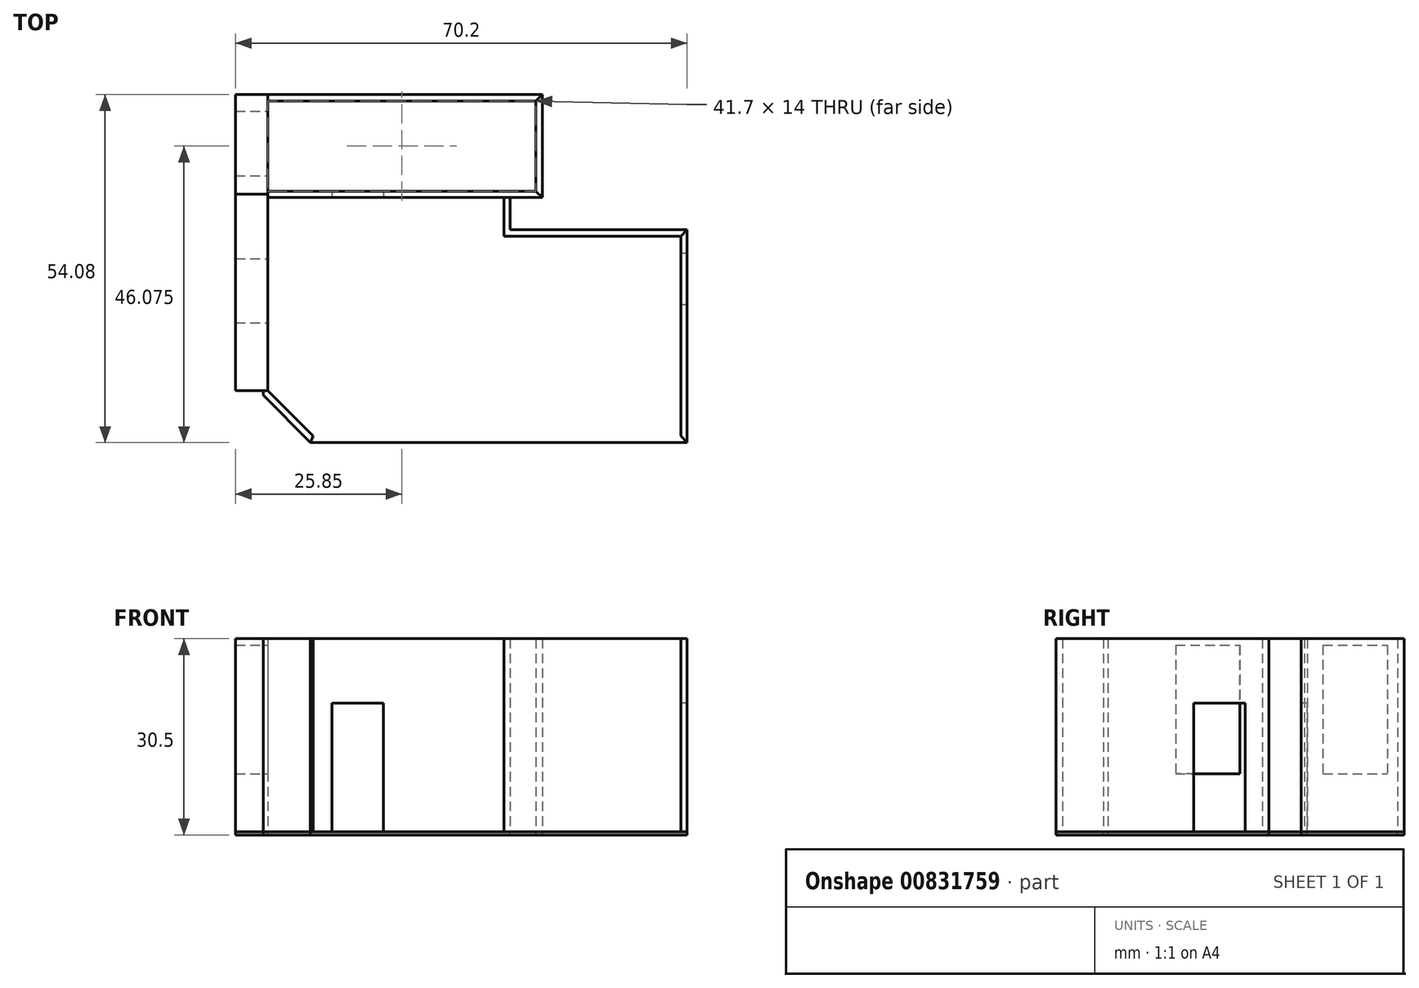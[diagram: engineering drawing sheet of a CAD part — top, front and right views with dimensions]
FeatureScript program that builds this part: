
annotation { "Feature Type Name" : "Feature", "Feature Type Description" : "" }
export const myFeature = defineFeature(function(context is Context, id is Id, definition is map)
    precondition{}
    {
        {
            var Q0;
            Q0=qCreatedBy(makeId("Top.planeOp"),FACE);
            var sketch = newSketch(context, id + "F0", { "sketchPlane" : qUnion([Q0])});
            skLineSegment(sketch, "E0", {"start": v(-36.7, -8.46) * mm, "end": v(-36.7, 21.54) * mm});
            skLineSegment(sketch, "E1", {"start": v(-36.7, 21.54) * mm, "end": v(0, 21.54) * mm});
            skLineSegment(sketch, "E2", {"start": v(0, 21.54) * mm, "end": v(0, 15.54) * mm});
            skLineSegment(sketch, "E3", {"start": v(0, 15.54) * mm, "end": v(27.5, 15.54) * mm});
            skLineSegment(sketch, "E4", {"start": v(27.5, 15.54) * mm, "end": v(27.5, -15.54) * mm});
            skLineSegment(sketch, "E5", {"start": v(27.5, -15.54) * mm, "end": v(-29.63, -15.54) * mm});
            skLineSegment(sketch, "E6", {"start": v(-29.63, -15.54) * mm, "end": v(-36.7, -8.46) * mm});
            skLineSegment(sketch, "E7", {"start": v(0, 15.54) * mm, "end": v(0, -15.54) * mm, "construction": true});
            skLineSegment(sketch, "E8", {"start": v(-36.7, 21.54) * mm, "end": v(-36.7, 36.54) * mm});
            skLineSegment(sketch, "E9", {"start": v(-36.7, 36.54) * mm, "end": v(5, 36.54) * mm});
            skLineSegment(sketch, "E10", {"start": v(5, 36.54) * mm, "end": v(5, 22.54) * mm});
            skLineSegment(sketch, "E11", {"start": v(5, 21.54) * mm, "end": v(0, 21.54) * mm});
            skLineSegment(sketch, "E12", {"start": v(-36.7, 22.54) * mm, "end": v(5, 22.54) * mm});
            skLineSegment(sketch, "E13.0", {"start": v(6, 37.54) * mm, "end": v(6, 21.54) * mm});
            skLineSegment(sketch, "E13.1", {"start": v(-36.7, 37.54) * mm, "end": v(6, 37.54) * mm});
            skLineSegment(sketch, "E14", {"start": v(-36.7, 37.54) * mm, "end": v(-36.7, 36.54) * mm});
            skLineSegment(sketch, "E15", {"start": v(6, 21.54) * mm, "end": v(5, 21.54) * mm});
            skLineSegment(sketch, "E16.0", {"start": v(-30.04, -16.54) * mm, "end": v(-37.4, -9.17) * mm});
            skLineSegment(sketch, "E16.1", {"start": v(1, 21.54) * mm, "end": v(1, 16.54) * mm});
            skLineSegment(sketch, "E16.2", {"start": v(1, 16.54) * mm, "end": v(28.5, 16.54) * mm});
            skLineSegment(sketch, "E16.3", {"start": v(28.5, 16.54) * mm, "end": v(28.5, -16.54) * mm});
            skLineSegment(sketch, "E16.4", {"start": v(28.5, -16.54) * mm, "end": v(-30.04, -16.54) * mm});
            skLineSegment(sketch, "E17", {"start": v(-36.7, -8.46) * mm, "end": v(-37.4, -9.17) * mm, "construction": true});
            skLineSegment(sketch, "E18", {"start": v(-36.7, 37.54) * mm, "end": v(-41.7, 37.54) * mm});
            skLineSegment(sketch, "E19", {"start": v(-41.7, 37.54) * mm, "end": v(-41.7, -8.46) * mm});
            skLineSegment(sketch, "E20", {"start": v(-41.7, -8.46) * mm, "end": v(-37.4, -8.46) * mm});
            skLineSegment(sketch, "E21", {"start": v(-37.4, -9.17) * mm, "end": v(-37.4, -8.46) * mm});
            skLineSegment(sketch, "E22", {"start": v(-29.63, -15.54) * mm, "end": v(-30.04, -16.54) * mm});
            skLineSegment(sketch, "E23", {"start": v(27.5, -15.54) * mm, "end": v(28.5, -16.54) * mm});
            skLineSegment(sketch, "E24", {"start": v(27.5, 15.54) * mm, "end": v(28.5, 16.54) * mm});
            skLineSegment(sketch, "E25", {"start": v(5, 22.54) * mm, "end": v(6, 21.54) * mm});
            skLineSegment(sketch, "E26", {"start": v(5, 36.54) * mm, "end": v(6, 37.54) * mm});
            skLineSegment(sketch, "E27", {"start": v(-36.7, 22.04) * mm, "end": v(-41.7, 22.04) * mm});
            skLineSegment(sketch, "E28", {"start": v(-36.7, 22.54) * mm, "end": v(-36.7, 21.54) * mm});
            skLineSegment(sketch, "E29", {"start": v(0, -15.54) * mm, "end": v(0, -16.54) * mm});
            skLineSegment(sketch, "E30", {"start": v(6, 21.54) * mm, "end": v(1, 21.54) * mm});
            skLineSegment(sketch, "E31", {"start": v(-37.4, -8.46) * mm, "end": v(-36.7, -8.46) * mm});
            skSolve(sketch);
        }
        {
            var Q0;
            Q0 = qSketchRegion(id + "F0", true);
            var Q1;
            Q1=makeQuery(id+"F0.imprint","IMPRINT",FACE,{"disambiguationData":[TD([[makeQuery(id+"F0.imprint","IMPRINT",EDGE,{"derivedFrom":sQuery(id+"F0.wireOp",EDGE,"E0")}),-1.0]])]});
            var Q2;
            Q2=makeQuery(id+"F0.imprint","IMPRINT",FACE,{"disambiguationData":[TD([[makeQuery(id+"F0.imprint","IMPRINT",EDGE,{"derivedFrom":sQuery(id+"F0.wireOp",EDGE,"E8")}),-1.0]])]});
            extrude(context, id + "F1", {"entities" : qUnion([Q0, Q1, Q2]), "oppositeDirection" : true, "depth" : 0.5 * mm, "offsetDistance" : 25 * mm});
        }
        {
            var Q0;
            {var subQ1=sQuery(id+"F0.wireOp",EDGE,"E0");Q0=makeQuery(id+"F0.imprint","IMPRINT",FACE,{"disambiguationData":[TD([[makeQuery(id+"F0.imprint","IMPRINT",EDGE,{"derivedFrom":subQ1}),1.0]])]});}
            extrude(context, id + "F2", {"entities" : qUnion([Q0]), "depth" : 30 * mm, "offsetDistance" : 25 * mm});
        }
        {
            var Q0;
            Q0=makeQuery(id+"F2.opExtrude","SWEPT_FACE",FACE,{"disambiguationData":[OSD([sQuery(id+"F0.wireOp",EDGE,"E0"),sQuery(id+"F0.wireOp",EDGE,"E28")])]});
            var sketch = newSketch(context, id + "F3", { "sketchPlane" : qUnion([Q0])});
            skLineSegment(sketch, "E32.bottom", {"start": v(2.04, 29) * mm, "end": v(12.04, 29) * mm});
            skLineSegment(sketch, "E32.top", {"start": v(2.04, 9) * mm, "end": v(12.04, 9) * mm});
            skLineSegment(sketch, "E32.left", {"start": v(2.04, 29) * mm, "end": v(2.04, 9) * mm});
            skLineSegment(sketch, "E32.right", {"start": v(12.04, 29) * mm, "end": v(12.04, 9) * mm});
            skLineSegment(sketch, "E33.0.0", {"start": v(-8.46, 0) * mm, "end": v(22.04, 0) * mm});
            skLineSegment(sketch, "E33.0.1", {"start": v(22.04, 0) * mm, "end": v(22.04, 30) * mm});
            skLineSegment(sketch, "E33.0.2", {"start": v(22.04, 30) * mm, "end": v(-8.46, 30) * mm});
            skLineSegment(sketch, "E33.0.3", {"start": v(-8.46, 30) * mm, "end": v(-8.46, 0) * mm});
            skSolve(sketch);
        }
        {
            var Q0;
            Q0=makeQuery(id+"F3.imprint","IMPRINT",FACE,{"disambiguationData":[TD([[makeQuery(id+"F3.imprint","IMPRINT",EDGE,{"derivedFrom":sQuery(id+"F3.wireOp",EDGE,"E32.bottom")}),-1.0]])]});
            extrude(context, id + "F4", {"entities" : qUnion([Q0]), "operationType" : NewBodyOperationType.REMOVE, "endBound" : BoundingType.UP_TO_NEXT, "oppositeDirection" : true, "depth" : 25 * mm, "offsetDistance" : 25 * mm});
        }
        {
            var Q0;
            {var subQ4=sQuery(id+"F0.wireOp",EDGE,"E8");Q0=makeQuery(id+"F0.imprint","IMPRINT",FACE,{"disambiguationData":[TD([[makeQuery(id+"F0.imprint","IMPRINT",EDGE,{"derivedFrom":subQ4}),1.0]])]});}
            extrude(context, id + "F5", {"entities" : qUnion([Q0]), "depth" : 30 * mm, "offsetDistance" : 25 * mm});
        }
        {
            var Q0;
            Q0=makeQuery(id+"F5.opExtrude","SWEPT_FACE",FACE,{"disambiguationData":[OSD([sQuery(id+"F0.wireOp",EDGE,"E8"),sQuery(id+"F0.wireOp",EDGE,"E14"),sQuery(id+"F0.wireOp",EDGE,"E28")])]});
            var sketch = newSketch(context, id + "F6", { "sketchPlane" : qUnion([Q0])});
            skLineSegment(sketch, "E34.bottom", {"start": v(24.94, 29) * mm, "end": v(34.94, 29) * mm});
            skLineSegment(sketch, "E34.top", {"start": v(24.94, 9) * mm, "end": v(34.94, 9) * mm});
            skLineSegment(sketch, "E34.left", {"start": v(24.94, 29) * mm, "end": v(24.94, 9) * mm});
            skLineSegment(sketch, "E34.right", {"start": v(34.94, 29) * mm, "end": v(34.94, 9) * mm});
            skLineSegment(sketch, "E35.0.0", {"start": v(22.04, 0) * mm, "end": v(37.54, 0) * mm});
            skLineSegment(sketch, "E35.0.1", {"start": v(37.54, 0) * mm, "end": v(37.54, 30) * mm});
            skLineSegment(sketch, "E35.0.2", {"start": v(37.54, 30) * mm, "end": v(22.04, 30) * mm});
            skLineSegment(sketch, "E35.0.3", {"start": v(22.04, 30) * mm, "end": v(22.04, 0) * mm});
            skLineSegment(sketch, "E36.0.0", {"start": v(2.04, 29) * mm, "end": v(2.04, 9) * mm});
            skLineSegment(sketch, "E36.0.1", {"start": v(2.04, 9) * mm, "end": v(12.04, 9) * mm});
            skLineSegment(sketch, "E36.0.2", {"start": v(12.04, 9) * mm, "end": v(12.04, 29) * mm});
            skLineSegment(sketch, "E36.0.3", {"start": v(12.04, 29) * mm, "end": v(2.04, 29) * mm});
            skSolve(sketch);
        }
        {
            var Q0;
            Q0=makeQuery(id+"F6.imprint","IMPRINT",FACE,{"disambiguationData":[TD([[makeQuery(id+"F6.imprint","IMPRINT",EDGE,{"derivedFrom":sQuery(id+"F6.wireOp",EDGE,"E34.bottom")}),-1.0]])]});
            extrude(context, id + "F7", {"entities" : qUnion([Q0]), "operationType" : NewBodyOperationType.REMOVE, "endBound" : BoundingType.UP_TO_NEXT, "oppositeDirection" : true, "depth" : 25 * mm, "offsetDistance" : 25 * mm});
        }
        {
            var Q0;
            Q0=makeQuery(id+"F0.imprint","IMPRINT",FACE,{"disambiguationData":[TD([[makeQuery(id+"F0.imprint","IMPRINT",EDGE,{"derivedFrom":sQuery(id+"F0.wireOp",EDGE,"E9")}),1.0]])]});
            extrude(context, id + "F8", {"entities" : qUnion([Q0]), "depth" : 30 * mm, "offsetDistance" : 25 * mm});
        }
        {
            var Q0;
            Q0=makeQuery(id+"F0.imprint","IMPRINT",FACE,{"disambiguationData":[TD([[makeQuery(id+"F0.imprint","IMPRINT",EDGE,{"derivedFrom":sQuery(id+"F0.wireOp",EDGE,"E10")}),1.0]])]});
            extrude(context, id + "F9", {"entities" : qUnion([Q0]), "depth" : 30 * mm, "offsetDistance" : 25 * mm});
        }
        {
            var Q0;
            {var subQ1=sQuery(id+"F0.wireOp",EDGE,"E1");Q0=makeQuery(id+"F0.imprint","IMPRINT",FACE,{"disambiguationData":[TD([[makeQuery(id+"F0.imprint","IMPRINT",EDGE,{"derivedFrom":subQ1}),1.0]])]});}
            extrude(context, id + "F10", {"entities" : qUnion([Q0]), "depth" : 30 * mm, "offsetDistance" : 25 * mm});
        }
        {
            var Q0;
            Q0=makeQuery(id+"F10.opExtrude","SWEPT_FACE",FACE,{"disambiguationData":[OSD([sQuery(id+"F0.wireOp",EDGE,"E1"),sQuery(id+"F0.wireOp",EDGE,"E11"),sQuery(id+"F0.wireOp",EDGE,"E15")])]});
            var sketch = newSketch(context, id + "F11", { "sketchPlane" : qUnion([Q0])});
            skLineSegment(sketch, "E37.bottom", {"start": v(-26.7, 0) * mm, "end": v(-18.7, 0) * mm});
            skLineSegment(sketch, "E37.top", {"start": v(-26.7, 20) * mm, "end": v(-18.7, 20) * mm});
            skLineSegment(sketch, "E37.left", {"start": v(-26.7, 0) * mm, "end": v(-26.7, 20) * mm});
            skLineSegment(sketch, "E37.right", {"start": v(-18.7, 0) * mm, "end": v(-18.7, 20) * mm});
            skLineSegment(sketch, "E38", {"start": v(-36.7, 30) * mm, "end": v(-36.7, 0) * mm});
            skSolve(sketch);
        }
        {
            var Q0;
            Q0=makeQuery(id+"F11.imprint","IMPRINT",FACE,{"disambiguationData":[TD([[makeQuery(id+"F11.imprint","IMPRINT",EDGE,{"derivedFrom":sQuery(id+"F11.wireOp",EDGE,"E37.bottom")}),1.0]])]});
            extrude(context, id + "F12", {"entities" : qUnion([Q0]), "operationType" : NewBodyOperationType.REMOVE, "endBound" : BoundingType.UP_TO_NEXT, "oppositeDirection" : true, "depth" : 25 * mm, "offsetDistance" : 25 * mm});
        }
        {
            var Q0;
            {var subQ1=sQuery(id+"F0.wireOp",EDGE,"E2");Q0=makeQuery(id+"F0.imprint","IMPRINT",FACE,{"disambiguationData":[TD([[makeQuery(id+"F0.imprint","IMPRINT",EDGE,{"derivedFrom":subQ1}),1.0]])]});}
            extrude(context, id + "F13", {"entities" : qUnion([Q0]), "depth" : 30 * mm, "offsetDistance" : 25 * mm});
        }
        {
            var Q0;
            Q0=makeQuery(id+"F0.imprint","IMPRINT",FACE,{"disambiguationData":[TD([[makeQuery(id+"F0.imprint","IMPRINT",EDGE,{"derivedFrom":sQuery(id+"F0.wireOp",EDGE,"E4")}),1.0]])]});
            extrude(context, id + "F14", {"entities" : qUnion([Q0]), "depth" : 30 * mm, "offsetDistance" : 25 * mm});
        }
        {
            var Q0;
            Q0=makeQuery(id+"F14.opExtrude","SWEPT_FACE",FACE,{"disambiguationData":[OSD([sQuery(id+"F0.wireOp",EDGE,"E4")])]});
            var sketch = newSketch(context, id + "F15", { "sketchPlane" : qUnion([Q0])});
            skLineSegment(sketch, "E39.bottom", {"start": v(-12.84, 0) * mm, "end": v(-4.84, 0) * mm});
            skLineSegment(sketch, "E39.top", {"start": v(-12.84, 20) * mm, "end": v(-4.84, 20) * mm});
            skLineSegment(sketch, "E39.left", {"start": v(-12.84, 0) * mm, "end": v(-12.84, 20) * mm});
            skLineSegment(sketch, "E39.right", {"start": v(-4.84, 0) * mm, "end": v(-4.84, 20) * mm});
            skLineSegment(sketch, "E40", {"start": v(-15.54, 0) * mm, "end": v(-15.54, 30) * mm});
            skSolve(sketch);
        }
        {
            var Q0;
            {var subQ1=sQuery(id+"F0.wireOp",EDGE,"E6");Q0=makeQuery(id+"F0.imprint","IMPRINT",FACE,{"disambiguationData":[TD([[makeQuery(id+"F0.imprint","IMPRINT",EDGE,{"derivedFrom":subQ1}),1.0]])]});}
            extrude(context, id + "F16", {"entities" : qUnion([Q0]), "depth" : 30 * mm, "offsetDistance" : 25 * mm});
        }
        {
            var Q0;
            Q0=makeQuery(id+"F15.imprint","IMPRINT",FACE,{"disambiguationData":[TD([[makeQuery(id+"F15.imprint","IMPRINT",EDGE,{"derivedFrom":sQuery(id+"F15.wireOp",EDGE,"E39.bottom")}),1.0]])]});
            extrude(context, id + "F17", {"entities" : qUnion([Q0]), "operationType" : NewBodyOperationType.REMOVE, "endBound" : BoundingType.UP_TO_NEXT, "oppositeDirection" : true, "depth" : 25 * mm, "offsetDistance" : 25 * mm});
        }
    });
